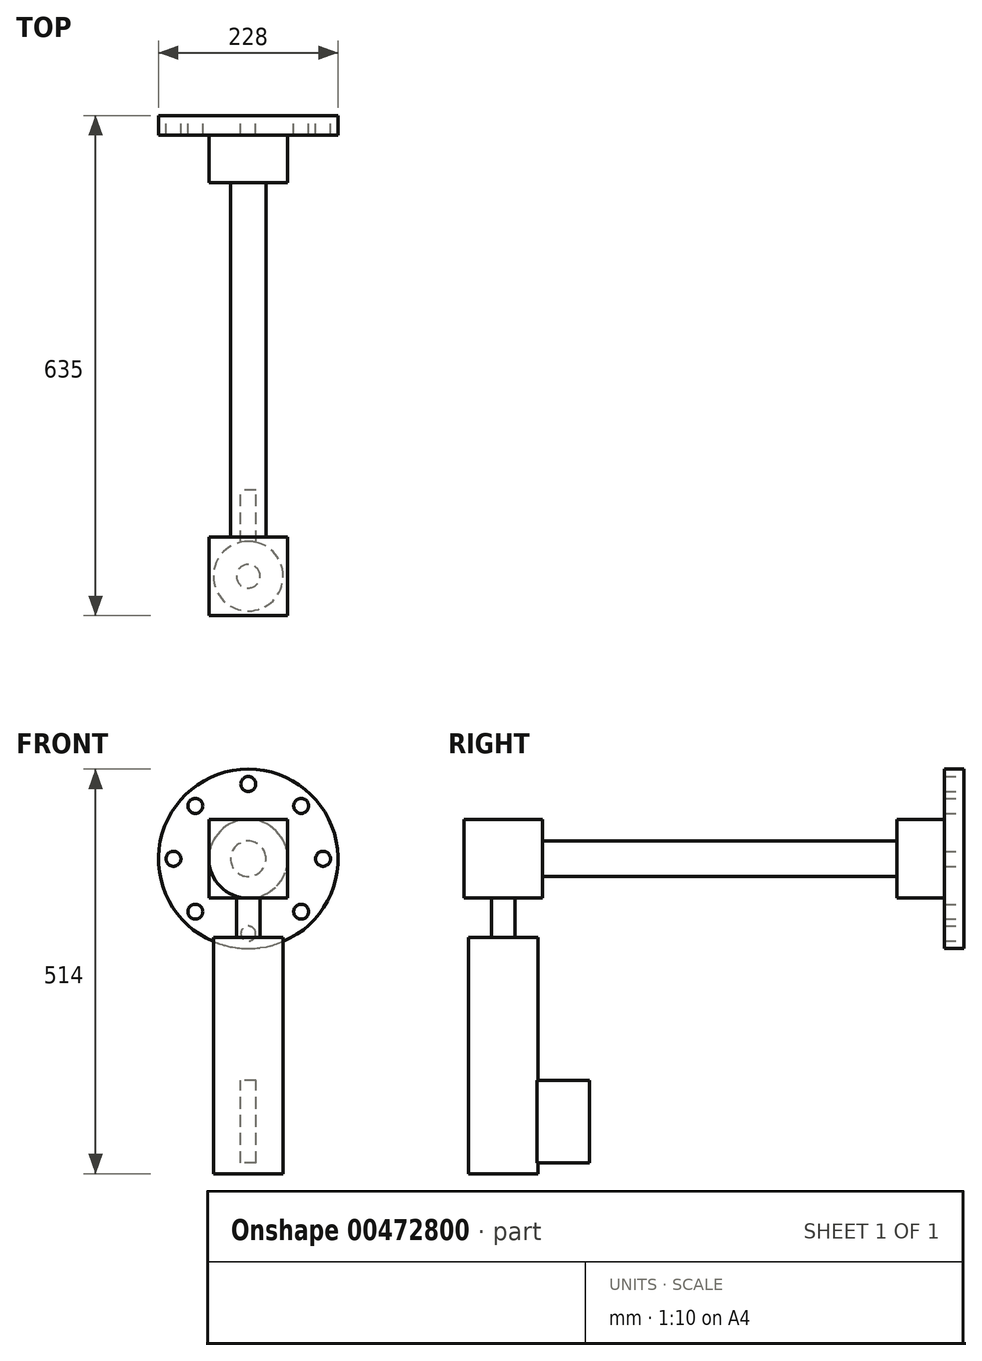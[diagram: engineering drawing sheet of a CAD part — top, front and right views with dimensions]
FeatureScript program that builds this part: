
annotation { "Feature Type Name" : "Feature", "Feature Type Description" : "" }
export const myFeature = defineFeature(function(context is Context, id is Id, definition is map)
    precondition{}
    {
        {
            var Q0;
            Q0=qCreatedBy(makeId("Front.planeOp"),FACE);
            var sketch = newSketch(context, id + "F0", { "sketchPlane" : qUnion([Q0])});
            skCircle(sketch, "E0", {"center": v(0, 0) * mm, "radius": 114 * mm});
            skCircle(sketch, "E1", {"center": v(95, 0) * mm, "radius": 9.5 * mm});
            skCircle(sketch, "E2.1.0", {"center": v(67.18, 67.18) * mm, "radius": 9.5 * mm});
            skCircle(sketch, "E2.2.0", {"center": v(0, 95) * mm, "radius": 9.5 * mm});
            skCircle(sketch, "E2.3.0", {"center": v(-67.18, 67.18) * mm, "radius": 9.5 * mm});
            skCircle(sketch, "E2.4.0", {"center": v(-95, 0) * mm, "radius": 9.5 * mm});
            skCircle(sketch, "E2.5.0", {"center": v(-67.18, -67.18) * mm, "radius": 9.5 * mm});
            skCircle(sketch, "E2.6.0", {"center": v(0, -95) * mm, "radius": 9.5 * mm});
            skCircle(sketch, "E2.7.0", {"center": v(67.18, -67.18) * mm, "radius": 9.5 * mm});
            skSolve(sketch);
        }
        {
            var Q0;
            Q0 = qSketchRegion(id + "F0", true);
            extrude(context, id + "F1", {"entities" : qUnion([Q0]), "depth" : 25 * mm});
        }
        {
            var Q0;
            Q0=makeQuery(id+"F1.opExtrude","CAP_FACE",FACE,{"disambiguationData":[OSD([sQuery(id+"F0.wireOp",EDGE,"E0"),sQuery(id+"F0.wireOp",EDGE,"E1"),sQuery(id+"F0.wireOp",EDGE,"E2.1.0"),sQuery(id+"F0.wireOp",EDGE,"E2.2.0"),sQuery(id+"F0.wireOp",EDGE,"E2.3.0"),sQuery(id+"F0.wireOp",EDGE,"E2.4.0"),sQuery(id+"F0.wireOp",EDGE,"E2.5.0"),sQuery(id+"F0.wireOp",EDGE,"E2.6.0"),sQuery(id+"F0.wireOp",EDGE,"E2.7.0")])],"isStart":false});
            var sketch = newSketch(context, id + "F2", { "sketchPlane" : qUnion([Q0])});
            skCircle(sketch, "E3", {"center": v(0, 0) * mm, "radius": 50 * mm});
            skSolve(sketch);
        }
        {
            var Q0;
            Q0 = qSketchRegion(id + "F2", true);
            extrude(context, id + "F3", {"entities" : qUnion([Q0]), "operationType" : NewBodyOperationType.ADD, "depth" : 60 * mm});
        }
        {
            var Q0;
            Q0=makeQuery(id+"F3.opExtrude","CAP_FACE",FACE,{"disambiguationData":[OSD([sQuery(id+"F2.wireOp",EDGE,"E3")])],"isStart":false});
            var sketch = newSketch(context, id + "F4", { "sketchPlane" : qUnion([Q0])});
            skCircle(sketch, "E4", {"center": v(0, 0) * mm, "radius": 22.5 * mm});
            skSolve(sketch);
        }
        {
            var Q0;
            Q0 = qSketchRegion(id + "F4", true);
            extrude(context, id + "F5", {"entities" : qUnion([Q0]), "operationType" : NewBodyOperationType.ADD, "depth" : 450 * mm});
        }
        {
            var Q0;
            Q0=makeQuery(id+"F5.opExtrude","CAP_FACE",FACE,{"disambiguationData":[OSD([sQuery(id+"F4.wireOp",EDGE,"E4")])],"isStart":false});
            var sketch = newSketch(context, id + "F6", { "sketchPlane" : qUnion([Q0])});
            skLineSegment(sketch, "E5.bottom", {"start": v(-50, 50) * mm, "end": v(50, 50) * mm});
            skLineSegment(sketch, "E5.top", {"start": v(-50, -50) * mm, "end": v(50, -50) * mm});
            skLineSegment(sketch, "E5.left", {"start": v(-50, 50) * mm, "end": v(-50, -50) * mm});
            skLineSegment(sketch, "E5.right", {"start": v(50, 50) * mm, "end": v(50, -50) * mm});
            skSolve(sketch);
        }
        {
            var Q0;
            Q0 = qSketchRegion(id + "F6", true);
            extrude(context, id + "F7", {"entities" : qUnion([Q0]), "operationType" : NewBodyOperationType.ADD, "depth" : 100 * mm});
        }
        {
            var Q0;
            Q0=makeQuery(id+"F7.opExtrude","SWEPT_FACE",FACE,{"disambiguationData":[OSD([sQuery(id+"F6.wireOp",EDGE,"E5.top")])]});
            var sketch = newSketch(context, id + "F8", { "sketchPlane" : qUnion([Q0])});
            skCircle(sketch, "E6", {"center": v(0, 585) * mm, "radius": 15 * mm});
            skPoint(sketch, "E6.centerSnap0", {"position": v(50, 585) * mm});
            skPoint(sketch, "E6.centerSnap1", {"position": v(0, 535) * mm});
            skSolve(sketch);
        }
        {
            var Q0;
            Q0 = qSketchRegion(id + "F8", true);
            extrude(context, id + "F9", {"entities" : qUnion([Q0]), "operationType" : NewBodyOperationType.ADD, "depth" : 50 * mm});
        }
        {
            var Q0;
            Q0=makeQuery(id+"F9.opExtrude","CAP_FACE",FACE,{"disambiguationData":[OSD([sQuery(id+"F8.wireOp",EDGE,"E6")])],"isStart":false});
            var sketch = newSketch(context, id + "F10", { "sketchPlane" : qUnion([Q0])});
            skCircle(sketch, "E7", {"center": v(0, 585) * mm, "radius": 44.19 * mm});
            skSolve(sketch);
        }
        {
            var Q0;
            Q0 = qSketchRegion(id + "F10", true);
            extrude(context, id + "F11", {"entities" : qUnion([Q0]), "operationType" : NewBodyOperationType.ADD, "depth" : 300 * mm});
        }
        {
            var Q0;
            Q0=qCreatedBy(makeId("Right.planeOp"),FACE);
            var sketch = newSketch(context, id + "F12", { "sketchPlane" : qUnion([Q0])});
            skLineSegment(sketch, "E8.bottom", {"start": v(-549.9, -281.37) * mm, "end": v(-475.31, -281.37) * mm});
            skLineSegment(sketch, "E8.top", {"start": v(-549.9, -386.44) * mm, "end": v(-475.31, -386.44) * mm});
            skLineSegment(sketch, "E8.left", {"start": v(-549.9, -281.37) * mm, "end": v(-549.9, -386.44) * mm});
            skLineSegment(sketch, "E8.right", {"start": v(-475.31, -281.37) * mm, "end": v(-475.31, -386.44) * mm});
            skSolve(sketch);
        }
        {
            var Q0;
            Q0 = qSketchRegion(id + "F12", true);
            extrude(context, id + "F13", {"entities" : qUnion([Q0]), "operationType" : NewBodyOperationType.ADD, "endBound" : BoundingType.SYMMETRIC, "depth" : 20 * mm});
        }
    });
